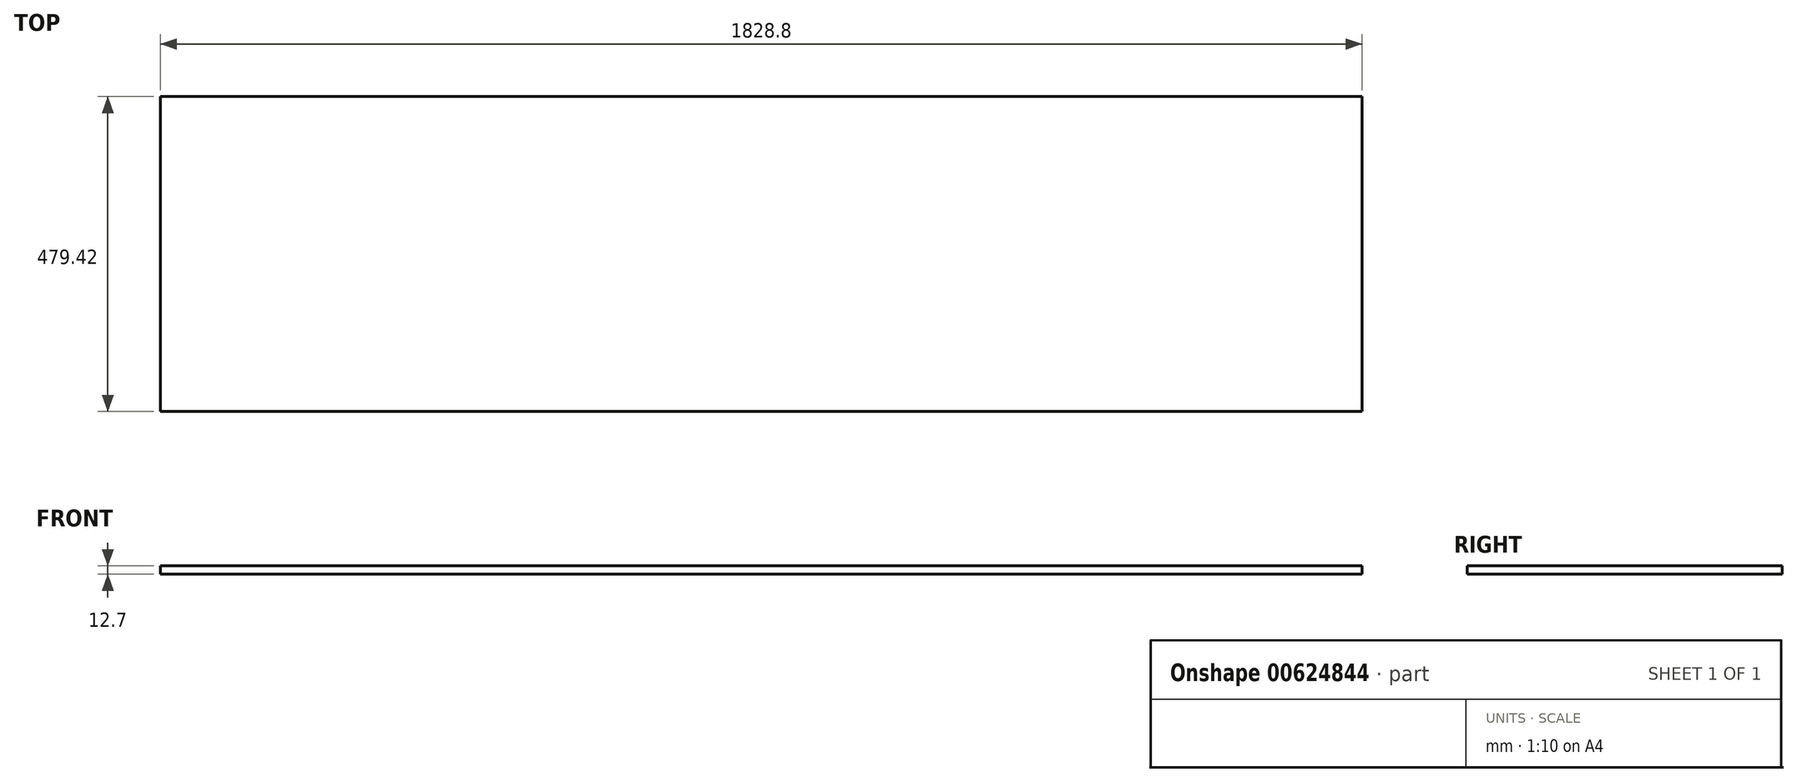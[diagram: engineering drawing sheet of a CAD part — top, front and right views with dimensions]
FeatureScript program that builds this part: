
annotation { "Feature Type Name" : "Feature", "Feature Type Description" : "" }
export const myFeature = defineFeature(function(context is Context, id is Id, definition is map)
    precondition{}
    {
        {
            var Q0;
            Q0=qCreatedBy(makeId("Top.planeOp"),FACE);
            var sketch = newSketch(context, id + "F0", { "sketchPlane" : qUnion([Q0])});
            skLineSegment(sketch, "E0.bottom", {"start": v(-914.4, 239.71) * mm, "end": v(914.4, 239.71) * mm});
            skLineSegment(sketch, "E0.top", {"start": v(-914.4, -239.71) * mm, "end": v(914.4, -239.71) * mm});
            skLineSegment(sketch, "E0.left", {"start": v(-914.4, 239.71) * mm, "end": v(-914.4, -239.71) * mm});
            skLineSegment(sketch, "E0.right", {"start": v(914.4, 239.71) * mm, "end": v(914.4, -239.71) * mm});
            skPoint(sketch, "E0.middle", {"position": v(0, 0) * mm});
            skSolve(sketch);
        }
        {
            var Q0;
            Q0 = qSketchRegion(id + "F0", true);
            extrude(context, id + "F1", {"entities" : qUnion([Q0]), "oppositeDirection" : true, "depth" : 12.7 * mm, "offsetDistance" : 25.4 * mm});
        }
    });
